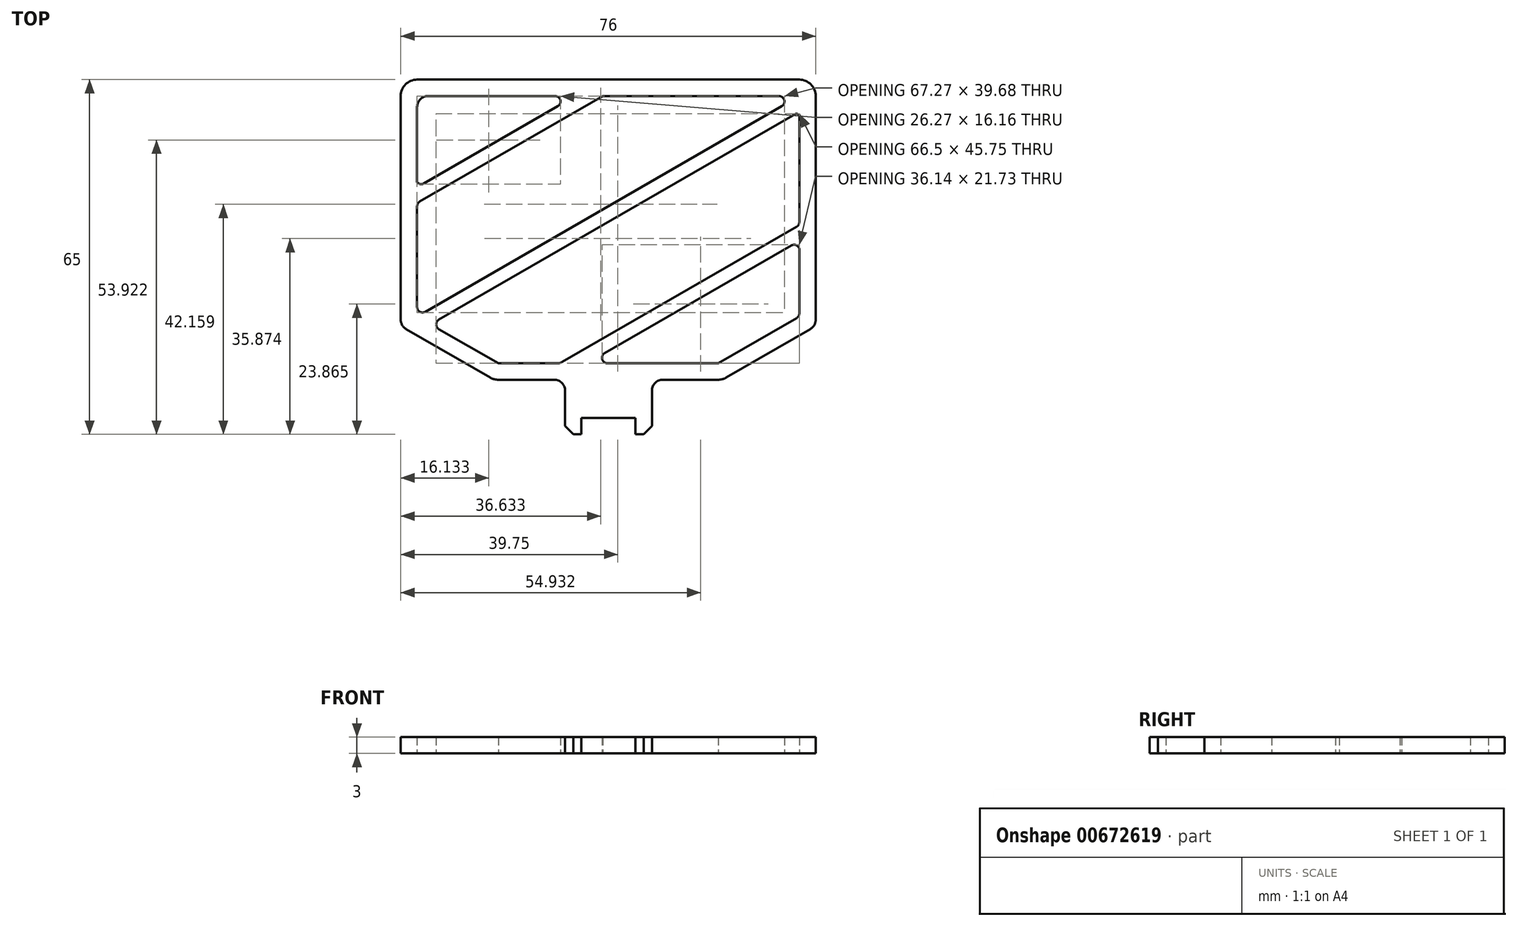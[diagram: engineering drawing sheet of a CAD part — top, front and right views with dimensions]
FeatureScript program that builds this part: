
annotation { "Feature Type Name" : "Feature", "Feature Type Description" : "" }
export const myFeature = defineFeature(function(context is Context, id is Id, definition is map)
    precondition{}
    {
        {
            var Q0;
            Q0=qCreatedBy(makeId("Top.planeOp"),FACE);
            var sketch = newSketch(context, id + "F0", { "sketchPlane" : qUnion([Q0])});
            skLineSegment(sketch, "E0.bottom", {"start": v(35, 27.5) * mm, "end": v(-35, 27.5) * mm});
            skLineSegment(sketch, "E0.top", {"start": v(20.13, -27.5) * mm, "end": v(10, -27.5) * mm});
            skLineSegment(sketch, "E0.left", {"start": v(38, 24.5) * mm, "end": v(38, -16.5) * mm});
            skLineSegment(sketch, "E0.right", {"start": v(-38, 24.5) * mm, "end": v(-38, -16.5) * mm});
            skPoint(sketch, "E0.middle", {"position": v(0, 0) * mm});
            skLineSegment(sketch, "E1", {"start": v(-4.9, -37.5) * mm, "end": v(-4.9, -34.5) * mm});
            skLineSegment(sketch, "E2", {"start": v(-7.9, -29.5) * mm, "end": v(-7.9, -36) * mm});
            skLineSegment(sketch, "E3", {"start": v(-6.4, -37.5) * mm, "end": v(-4.9, -37.5) * mm});
            skLineSegment(sketch, "E4", {"start": v(5, -37.5) * mm, "end": v(5, -34.5) * mm});
            skLineSegment(sketch, "E5", {"start": v(8, -29.5) * mm, "end": v(8, -36) * mm});
            skLineSegment(sketch, "E6", {"start": v(6.5, -37.5) * mm, "end": v(5, -37.5) * mm});
            skLineSegment(sketch, "E7.0", {"start": v(-35, 22.5) * mm, "end": v(-35, -14.18) * mm});
            skLineSegment(sketch, "E7.1", {"start": v(-9.73, 24.5) * mm, "end": v(-33, 24.5) * mm});
            skLineSegment(sketch, "E7.2", {"start": v(35, 20.75) * mm, "end": v(35, 1.4) * mm});
            skLineSegment(sketch, "E7.3", {"start": v(20.13, -24.5) * mm, "end": v(-0.14, -24.5) * mm});
            skPoint(sketch, "E8.visualSharp", {"position": v(-38, 27.5) * mm});
            skArc(sketch, "E8.filletArc", {"start": v(-35, 27.5) * mm, "mid": v(-37.12, 26.62) * mm, "end": v(-38, 24.5) * mm});
            skPoint(sketch, "E9.visualSharp", {"position": v(38, 27.5) * mm});
            skArc(sketch, "E9.filletArc", {"start": v(38, 24.5) * mm, "mid": v(37.12, 26.62) * mm, "end": v(35, 27.5) * mm});
            skLineSegment(sketch, "E10", {"start": v(-35.25, 24.5) * mm, "end": v(-35.25, 9.34) * mm});
            skLineSegment(sketch, "E11", {"start": v(-35, 4.3) * mm, "end": v(-35, -7.5) * mm});
            skLineSegment(sketch, "E12", {"start": v(-35, -7.5) * mm, "end": v(-35, -7.5) * mm});
            skLineSegment(sketch, "E13", {"start": v(-33.75, 8.48) * mm, "end": v(-9.23, 22.63) * mm});
            skLineSegment(sketch, "E14.0", {"start": v(-34.5, 5.16) * mm, "end": v(-1, 24.5) * mm});
            skLineSegment(sketch, "E15.0", {"start": v(-33.5, -15.05) * mm, "end": v(31.77, 22.63) * mm});
            skLineSegment(sketch, "E16.0", {"start": v(-31, -16.5) * mm, "end": v(34.25, 21.18) * mm});
            skLineSegment(sketch, "E17.0", {"start": v(-8.4, -24.23) * mm, "end": v(34.5, 0.54) * mm});
            skLineSegment(sketch, "E18.0", {"start": v(-0.64, -22.63) * mm, "end": v(33.54, -2.9) * mm});
            skPoint(sketch, "E19.startSnap0", {"position": v(0, -27.5) * mm});
            skLineSegment(sketch, "E20", {"start": v(0, -34.5) * mm, "end": v(-4.9, -34.5) * mm});
            skLineSegment(sketch, "E21", {"start": v(-4.9, -34.5) * mm, "end": v(5, -34.5) * mm});
            skLineSegment(sketch, "E22", {"start": v(-7.9, -36) * mm, "end": v(-6.4, -37.5) * mm});
            skLineSegment(sketch, "E23", {"start": v(6.5, -37.5) * mm, "end": v(8, -36) * mm});
            skLineSegment(sketch, "E24.trimOffspring", {"start": v(-9.9, -27.5) * mm, "end": v(-18.13, -27.5) * mm});
            skPoint(sketch, "E25.end.orphan", {"position": v(-5, -29.5) * mm});
            skPoint(sketch, "E26.orphan", {"position": v(5, -27.5) * mm});
            skPoint(sketch, "E27.orphan", {"position": v(8, -37.5) * mm});
            skPoint(sketch, "E28.orphan", {"position": v(-7.9, -37.5) * mm});
            skPoint(sketch, "E29.visualSharp", {"position": v(-7.9, -27.5) * mm});
            skArc(sketch, "E29.filletArc", {"start": v(-7.9, -29.5) * mm, "mid": v(-8.49, -28.09) * mm, "end": v(-9.9, -27.5) * mm});
            skPoint(sketch, "E30.visualSharp", {"position": v(8, -27.5) * mm});
            skArc(sketch, "E30.filletArc", {"start": v(10, -27.5) * mm, "mid": v(8.59, -28.09) * mm, "end": v(8, -29.5) * mm});
            skPoint(sketch, "E31.visualSharp", {"position": v(38, -27.5) * mm});
            skPoint(sketch, "E32.visualSharp", {"position": v(-38, -27.5) * mm});
            skArc(sketch, "E33.filletArc", {"start": v(-9.23, 22.63) * mm, "mid": v(-8.77, 23.76) * mm, "end": v(-9.73, 24.5) * mm});
            skArc(sketch, "E34.filletArc", {"start": v(-0.64, -22.63) * mm, "mid": v(-1.1, -23.76) * mm, "end": v(-0.14, -24.5) * mm});
            skLineSegment(sketch, "E35", {"start": v(-9.4, -24.5) * mm, "end": v(-20.13, -24.5) * mm});
            skPoint(sketch, "E36.visualSharp", {"position": v(-35.25, 7.61) * mm});
            skArc(sketch, "E36.filletArc", {"start": v(-35.25, 9.34) * mm, "mid": v(-34.75, 8.48) * mm, "end": v(-33.75, 8.48) * mm});
            skArc(sketch, "E37.filletArc", {"start": v(-34.5, 5.16) * mm, "mid": v(-34.87, 4.8) * mm, "end": v(-35, 4.3) * mm});
            skArc(sketch, "E38.filletArc", {"start": v(-35, -14.18) * mm, "mid": v(-34.5, -15.05) * mm, "end": v(-33.5, -15.05) * mm});
            skPoint(sketch, "E39.visualSharp", {"position": v(-8.87, -24.5) * mm});
            skArc(sketch, "E39.filletArc", {"start": v(-9.4, -24.5) * mm, "mid": v(-8.89, -24.43) * mm, "end": v(-8.4, -24.23) * mm});
            skArc(sketch, "E40.filletArc", {"start": v(34.5, 0.54) * mm, "mid": v(34.87, 0.9) * mm, "end": v(35, 1.4) * mm});
            skLineSegment(sketch, "E41", {"start": v(-1, 24.5) * mm, "end": v(31.27, 24.5) * mm});
            skArc(sketch, "E42.filletArc", {"start": v(31.77, 22.63) * mm, "mid": v(32.23, 23.76) * mm, "end": v(31.27, 24.5) * mm});
            skArc(sketch, "E43.filletArc", {"start": v(35, 20.75) * mm, "mid": v(34.75, 21.18) * mm, "end": v(34.25, 21.18) * mm});
            skPoint(sketch, "E44.visualSharp", {"position": v(35, -2.06) * mm});
            skArc(sketch, "E44.filletArc", {"start": v(35, -3.5) * mm, "mid": v(34.41, -2.84) * mm, "end": v(33.54, -2.9) * mm});
            skLineSegment(sketch, "E45.0", {"start": v(5, -36.7) * mm, "end": v(5.36, -36.5) * mm});
            skPoint(sketch, "E46.orphan", {"position": v(38.53, -24.5) * mm});
            skLineSegment(sketch, "E47.trimOffspring", {"start": v(21.63, -27.1) * mm, "end": v(37, -18.22) * mm});
            skLineSegment(sketch, "E48.0", {"start": v(20.13, -24.5) * mm, "end": v(34.5, -16.2) * mm});
            skPoint(sketch, "E49.visualSharp", {"position": v(20.93, -27.5) * mm});
            skArc(sketch, "E49.filletArc", {"start": v(20.13, -27.5) * mm, "mid": v(20.9, -27.4) * mm, "end": v(21.63, -27.1) * mm});
            skPoint(sketch, "E50.visualSharp", {"position": v(38, -17.65) * mm});
            skArc(sketch, "E50.filletArc", {"start": v(37, -18.22) * mm, "mid": v(37.73, -17.5) * mm, "end": v(38, -16.5) * mm});
            skLineSegment(sketch, "E51", {"start": v(-9.9, -27.5) * mm, "end": v(-20.13, -27.5) * mm});
            skLineSegment(sketch, "E52", {"start": v(-31, -18.22) * mm, "end": v(-20.13, -24.5) * mm});
            skLineSegment(sketch, "E53.MirrorCS", {"start": v(-20.13, -24.5) * mm, "end": v(-31, -18.22) * mm});
            skLineSegment(sketch, "E54.MirrorCS", {"start": v(-21.63, -27.1) * mm, "end": v(-37, -18.22) * mm});
            skPoint(sketch, "E55.orphan", {"position": v(-18.13, -27.5) * mm});
            skPoint(sketch, "E56.start.orphan", {"position": v(0, -25.67) * mm});
            skLineSegment(sketch, "E57", {"start": v(-37, -18.22) * mm, "end": v(-21.63, -27.1) * mm});
            skPoint(sketch, "E58.visualSharp", {"position": v(-38, -17.65) * mm});
            skArc(sketch, "E58.filletArc", {"start": v(-38, -16.5) * mm, "mid": v(-37.73, -17.5) * mm, "end": v(-37, -18.22) * mm});
            skPoint(sketch, "E59.visualSharp", {"position": v(-20.93, -27.5) * mm});
            skArc(sketch, "E59.filletArc", {"start": v(-21.63, -27.1) * mm, "mid": v(-20.9, -27.4) * mm, "end": v(-20.13, -27.5) * mm});
            skPoint(sketch, "E60.start.orphan", {"position": v(-21.63, -27.1) * mm});
            skPoint(sketch, "E61.orphan", {"position": v(-37, -14.76) * mm});
            skPoint(sketch, "E62.visualSharp", {"position": v(-32.5, -17.36) * mm});
            skArc(sketch, "E62.filletArc", {"start": v(-31, -16.5) * mm, "mid": v(-31.5, -17.36) * mm, "end": v(-31, -18.22) * mm});
            skArc(sketch, "E63.filletArc", {"start": v(-33, 24.5) * mm, "mid": v(-34.41, 23.91) * mm, "end": v(-35, 22.5) * mm});
            skLineSegment(sketch, "E64", {"start": v(0, -27.5) * mm, "end": v(0, -34.5) * mm, "construction": true});
            skPoint(sketch, "E65.endSnap0", {"position": v(34.41, -2.84) * mm});
            skLineSegment(sketch, "E66", {"start": v(35, -3.5) * mm, "end": v(35, -15.34) * mm});
            skPoint(sketch, "E67.orphan", {"position": v(37, -14.76) * mm});
            skPoint(sketch, "E68.visualSharp", {"position": v(35, -15.91) * mm});
            skArc(sketch, "E68.filletArc", {"start": v(34.5, -16.2) * mm, "mid": v(34.87, -15.84) * mm, "end": v(35, -15.34) * mm});
            skSolve(sketch);
        }
        {
            var Q0;
            Q0=makeQuery(id+"F0.imprint","IMPRINT",FACE,{"disambiguationData":[TD([[makeQuery(id+"F0.imprint","IMPRINT",EDGE,{"derivedFrom":sQuery(id+"F0.wireOp",EDGE,"E0.bottom")}),1.0]])]});
            extrude(context, id + "F1", {"entities" : qUnion([Q0]), "depth" : 3 * mm, "offsetDistance" : 25 * mm});
        }
    });
